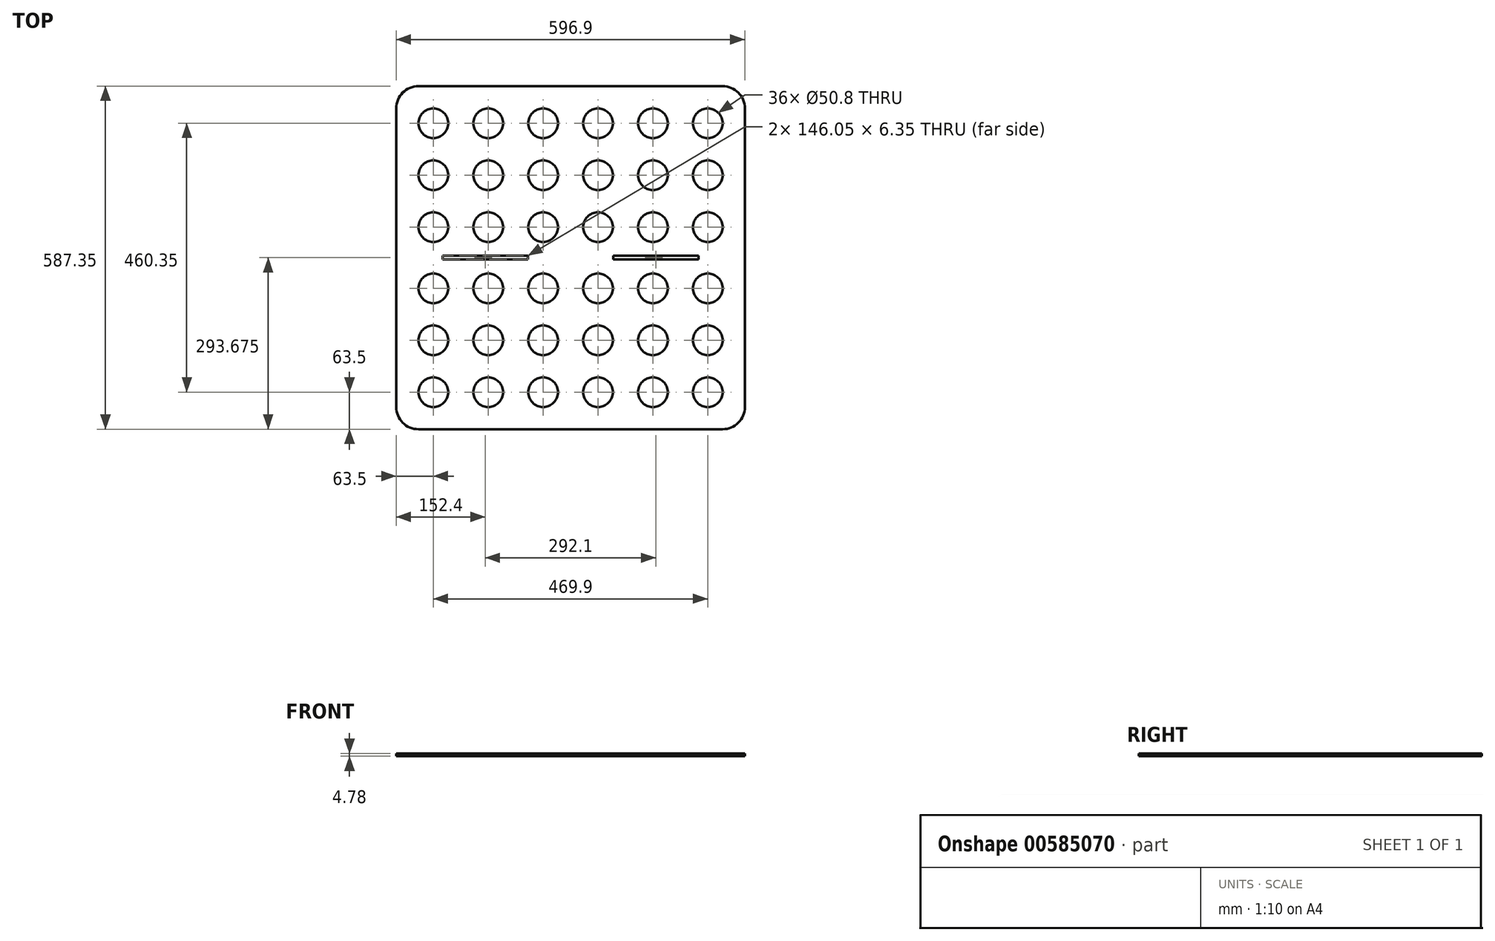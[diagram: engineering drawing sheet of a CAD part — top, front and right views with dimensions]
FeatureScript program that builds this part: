
annotation { "Feature Type Name" : "Feature", "Feature Type Description" : "" }
export const myFeature = defineFeature(function(context is Context, id is Id, definition is map)
    precondition{}
    {
        {
            var Q0;
            Q0=qCreatedBy(makeId("Top.planeOp"),FACE);
            var sketch = newSketch(context, id + "F0", { "sketchPlane" : qUnion([Q0])});
            skCircle(sketch, "E0", {"center": v(533.4, 346.05) * mm, "radius": 25.4 * mm});
            skLineSegment(sketch, "E1.bottom", {"start": v(0, 0) * mm, "end": v(596.9, 0) * mm});
            skLineSegment(sketch, "E1.top", {"start": v(0, 587.35) * mm, "end": v(596.9, 587.35) * mm});
            skLineSegment(sketch, "E1.left", {"start": v(0, 0) * mm, "end": v(0, 587.35) * mm});
            skLineSegment(sketch, "E1.right", {"start": v(596.9, 0) * mm, "end": v(596.9, 587.35) * mm});
            skLineSegment(sketch, "E2", {"start": v(298.45, 587.35) * mm, "end": v(298.45, 0) * mm, "construction": true});
            skCircle(sketch, "E3.1.0.1", {"center": v(439.42, 346.05) * mm, "radius": 25.4 * mm});
            skCircle(sketch, "E3.2.0.1", {"center": v(345.44, 346.05) * mm, "radius": 25.4 * mm});
            skCircle(sketch, "E3.3.0.1", {"center": v(251.46, 346.05) * mm, "radius": 25.4 * mm});
            skCircle(sketch, "E3.4.0.1", {"center": v(157.48, 346.05) * mm, "radius": 25.4 * mm});
            skCircle(sketch, "E3.5.0.1", {"center": v(63.5, 346.05) * mm, "radius": 25.4 * mm});
            skLineSegment(sketch, "E3.direction1", {"start": v(0, 0) * mm, "end": v(-88.9, 0) * mm, "construction": true});
            skLineSegment(sketch, "E4", {"start": v(0, 293.67) * mm, "end": v(596.9, 293.67) * mm, "construction": true});
            skCircle(sketch, "E5.0.1.0", {"center": v(157.48, 434.95) * mm, "radius": 25.4 * mm});
            skCircle(sketch, "E5.0.1.1", {"center": v(439.42, 434.95) * mm, "radius": 25.4 * mm});
            skCircle(sketch, "E5.0.1.2", {"center": v(251.46, 434.95) * mm, "radius": 25.4 * mm});
            skCircle(sketch, "E5.0.1.3", {"center": v(63.5, 434.95) * mm, "radius": 25.4 * mm});
            skCircle(sketch, "E5.0.1.4", {"center": v(533.4, 434.95) * mm, "radius": 25.4 * mm});
            skCircle(sketch, "E5.0.1.5", {"center": v(345.44, 434.95) * mm, "radius": 25.4 * mm});
            skCircle(sketch, "E5.0.2.0", {"center": v(157.48, 523.85) * mm, "radius": 25.4 * mm});
            skCircle(sketch, "E5.0.2.1", {"center": v(439.42, 523.85) * mm, "radius": 25.4 * mm});
            skCircle(sketch, "E5.0.2.2", {"center": v(251.46, 523.85) * mm, "radius": 25.4 * mm});
            skCircle(sketch, "E5.0.2.3", {"center": v(63.5, 523.85) * mm, "radius": 25.4 * mm});
            skCircle(sketch, "E5.0.2.4", {"center": v(533.4, 523.85) * mm, "radius": 25.4 * mm});
            skCircle(sketch, "E5.0.2.5", {"center": v(345.44, 523.85) * mm, "radius": 25.4 * mm});
            skLineSegment(sketch, "E5.direction1", {"start": v(63.5, 346.05) * mm, "end": v(88.9, 346.05) * mm, "construction": true});
            skLineSegment(sketch, "E5.direction2", {"start": v(63.5, 346.05) * mm, "end": v(63.5, 434.95) * mm, "construction": true});
            skCircle(sketch, "E6.0.1.0", {"center": v(439.42, 63.5) * mm, "radius": 25.4 * mm});
            skCircle(sketch, "E6.0.1.1", {"center": v(251.46, 241.3) * mm, "radius": 25.4 * mm});
            skLineSegment(sketch, "E6.0.1.2", {"start": v(63.5, 63.5) * mm, "end": v(63.5, 152.4) * mm, "construction": true});
            skCircle(sketch, "E6.0.1.3", {"center": v(345.44, 152.4) * mm, "radius": 25.4 * mm});
            skCircle(sketch, "E6.0.1.4", {"center": v(157.48, 241.3) * mm, "radius": 25.4 * mm});
            skCircle(sketch, "E6.0.1.5", {"center": v(251.46, 63.5) * mm, "radius": 25.4 * mm});
            skCircle(sketch, "E6.0.1.6", {"center": v(533.4, 63.5) * mm, "radius": 25.4 * mm});
            skCircle(sketch, "E6.0.1.7", {"center": v(439.42, 241.3) * mm, "radius": 25.4 * mm});
            skCircle(sketch, "E6.0.1.8", {"center": v(63.5, 241.3) * mm, "radius": 25.4 * mm});
            skCircle(sketch, "E6.0.1.9", {"center": v(345.44, 63.5) * mm, "radius": 25.4 * mm});
            skCircle(sketch, "E6.0.1.10", {"center": v(345.44, 241.3) * mm, "radius": 25.4 * mm});
            skCircle(sketch, "E6.0.1.11", {"center": v(439.42, 152.4) * mm, "radius": 25.4 * mm});
            skCircle(sketch, "E6.0.1.12", {"center": v(63.5, 152.4) * mm, "radius": 25.4 * mm});
            skCircle(sketch, "E6.0.1.13", {"center": v(157.48, 152.4) * mm, "radius": 25.4 * mm});
            skCircle(sketch, "E6.0.1.14", {"center": v(63.5, 63.5) * mm, "radius": 25.4 * mm});
            skCircle(sketch, "E6.0.1.15", {"center": v(533.4, 152.4) * mm, "radius": 25.4 * mm});
            skCircle(sketch, "E6.0.1.16", {"center": v(157.48, 63.5) * mm, "radius": 25.4 * mm});
            skCircle(sketch, "E6.0.1.17", {"center": v(251.46, 152.4) * mm, "radius": 25.4 * mm});
            skCircle(sketch, "E6.0.1.18", {"center": v(533.4, 241.3) * mm, "radius": 25.4 * mm});
            skLineSegment(sketch, "E6.0.1.19", {"start": v(63.5, 63.5) * mm, "end": v(88.9, 63.5) * mm, "construction": true});
            skLineSegment(sketch, "E6.0.1.20", {"start": v(63.5, 63.5) * mm, "end": v(88.9, 63.5) * mm, "construction": true});
            skLineSegment(sketch, "E6.direction2", {"start": v(63.5, 346.05) * mm, "end": v(63.5, 65.07) * mm, "construction": true});
            skSolve(sketch);
        }
        {
            var Q0;
            Q0 = qSketchRegion(id + "F0", true);
            extrude(context, id + "F1", {"entities" : qUnion([Q0]), "depth" : 4.78 * mm, "offsetDistance" : 25.4 * mm});
        }
        {
            var Q0;
            Q0=makeQuery(id+"F1.opExtrude","SWEPT_EDGE",EDGE,{"disambiguationData":[OSD([sQuery(id+"F0.wireOp",EDGE,"E1.bottom"),sQuery(id+"F0.wireOp",EDGE,"E1.left")])]});
            var Q1;
            Q1=makeQuery(id+"F1.opExtrude","SWEPT_EDGE",EDGE,{"disambiguationData":[OSD([sQuery(id+"F0.wireOp",EDGE,"E1.bottom"),sQuery(id+"F0.wireOp",EDGE,"E1.right")])]});
            var Q2;
            Q2=makeQuery(id+"F1.opExtrude","SWEPT_EDGE",EDGE,{"disambiguationData":[OSD([sQuery(id+"F0.wireOp",EDGE,"E1.top"),sQuery(id+"F0.wireOp",EDGE,"E1.right")])]});
            var Q3;
            Q3=makeQuery(id+"F1.opExtrude","SWEPT_EDGE",EDGE,{"disambiguationData":[OSD([sQuery(id+"F0.wireOp",EDGE,"E1.top"),sQuery(id+"F0.wireOp",EDGE,"E1.left")])]});
            fillet(context, id + "F2", {"entities" : qUnion([Q0, Q1, Q2, Q3]), "radius" : 38.1 * mm, "tangentPropagation" : true, "allowEdgeOverflow" : false});
        }
        {
            var Q0;
            Q0=makeQuery(id+"F1.opExtrude","CAP_FACE",FACE,{"disambiguationData":[OSD([sQuery(id+"F0.wireOp",EDGE,"E0"),sQuery(id+"F0.wireOp",EDGE,"E1.bottom"),sQuery(id+"F0.wireOp",EDGE,"E1.top"),sQuery(id+"F0.wireOp",EDGE,"E1.left"),sQuery(id+"F0.wireOp",EDGE,"E1.right"),sQuery(id+"F0.wireOp",EDGE,"E3.1.0.1"),sQuery(id+"F0.wireOp",EDGE,"E3.2.0.1"),sQuery(id+"F0.wireOp",EDGE,"E3.3.0.1"),sQuery(id+"F0.wireOp",EDGE,"E3.4.0.1"),sQuery(id+"F0.wireOp",EDGE,"E3.5.0.1"),sQuery(id+"F0.wireOp",EDGE,"E5.0.1.0"),sQuery(id+"F0.wireOp",EDGE,"E5.0.1.1"),sQuery(id+"F0.wireOp",EDGE,"E5.0.1.2"),sQuery(id+"F0.wireOp",EDGE,"E5.0.1.3"),sQuery(id+"F0.wireOp",EDGE,"E5.0.1.4"),sQuery(id+"F0.wireOp",EDGE,"E5.0.1.5"),sQuery(id+"F0.wireOp",EDGE,"E5.0.2.0"),sQuery(id+"F0.wireOp",EDGE,"E5.0.2.1"),sQuery(id+"F0.wireOp",EDGE,"E5.0.2.2"),sQuery(id+"F0.wireOp",EDGE,"E5.0.2.3"),sQuery(id+"F0.wireOp",EDGE,"E5.0.2.4"),sQuery(id+"F0.wireOp",EDGE,"E5.0.2.5"),sQuery(id+"F0.wireOp",EDGE,"4111b35f-3c82-41cd-824e-7dc98a569e06.0.1.0"),sQuery(id+"F0.wireOp",EDGE,"4111b35f-3c82-41cd-824e-7dc98a569e06.0.1.1"),sQuery(id+"F0.wireOp",EDGE,"4111b35f-3c82-41cd-824e-7dc98a569e06.0.1.3"),sQuery(id+"F0.wireOp",EDGE,"4111b35f-3c82-41cd-824e-7dc98a569e06.0.1.4"),sQuery(id+"F0.wireOp",EDGE,"4111b35f-3c82-41cd-824e-7dc98a569e06.0.1.5"),sQuery(id+"F0.wireOp",EDGE,"4111b35f-3c82-41cd-824e-7dc98a569e06.0.1.6"),sQuery(id+"F0.wireOp",EDGE,"4111b35f-3c82-41cd-824e-7dc98a569e06.0.1.7"),sQuery(id+"F0.wireOp",EDGE,"4111b35f-3c82-41cd-824e-7dc98a569e06.0.1.8"),sQuery(id+"F0.wireOp",EDGE,"4111b35f-3c82-41cd-824e-7dc98a569e06.0.1.9"),sQuery(id+"F0.wireOp",EDGE,"4111b35f-3c82-41cd-824e-7dc98a569e06.0.1.10"),sQuery(id+"F0.wireOp",EDGE,"4111b35f-3c82-41cd-824e-7dc98a569e06.0.1.11"),sQuery(id+"F0.wireOp",EDGE,"4111b35f-3c82-41cd-824e-7dc98a569e06.0.1.12"),sQuery(id+"F0.wireOp",EDGE,"4111b35f-3c82-41cd-824e-7dc98a569e06.0.1.13"),sQuery(id+"F0.wireOp",EDGE,"4111b35f-3c82-41cd-824e-7dc98a569e06.0.1.14"),sQuery(id+"F0.wireOp",EDGE,"4111b35f-3c82-41cd-824e-7dc98a569e06.0.1.15"),sQuery(id+"F0.wireOp",EDGE,"4111b35f-3c82-41cd-824e-7dc98a569e06.0.1.16"),sQuery(id+"F0.wireOp",EDGE,"4111b35f-3c82-41cd-824e-7dc98a569e06.0.1.17"),sQuery(id+"F0.wireOp",EDGE,"4111b35f-3c82-41cd-824e-7dc98a569e06.0.1.18")])],"isStart":false});
            var sketch = newSketch(context, id + "F3", { "sketchPlane" : qUnion([Q0])});
            skLineSegment(sketch, "E7", {"start": v(0, 293.67) * mm, "end": v(596.9, 293.67) * mm, "construction": true});
            skLineSegment(sketch, "E8", {"start": v(298.45, 587.35) * mm, "end": v(298.45, 293.67) * mm, "construction": true});
            skLineSegment(sketch, "E9.bottom", {"start": v(225.42, 296.85) * mm, "end": v(79.37, 296.85) * mm});
            skLineSegment(sketch, "E9.top", {"start": v(225.42, 290.5) * mm, "end": v(79.37, 290.5) * mm});
            skLineSegment(sketch, "E9.left", {"start": v(225.42, 296.85) * mm, "end": v(225.42, 290.5) * mm});
            skLineSegment(sketch, "E9.right", {"start": v(79.37, 296.85) * mm, "end": v(79.37, 290.5) * mm});
            skPoint(sketch, "E9.middle", {"position": v(152.4, 293.67) * mm});
            skLineSegment(sketch, "E10.1.0.0", {"start": v(517.52, 290.5) * mm, "end": v(371.47, 290.5) * mm});
            skLineSegment(sketch, "E10.1.0.1", {"start": v(517.52, 296.85) * mm, "end": v(371.47, 296.85) * mm});
            skPoint(sketch, "E10.1.0.2", {"position": v(439.17, 293.67) * mm});
            skLineSegment(sketch, "E10.1.0.3", {"start": v(517.52, 296.85) * mm, "end": v(517.52, 290.5) * mm});
            skLineSegment(sketch, "E10.1.0.4", {"start": v(371.47, 296.85) * mm, "end": v(371.47, 290.5) * mm});
            skSolve(sketch);
        }
        {
            var Q0;
            Q0 = qSketchRegion(id + "F3", true);
            extrude(context, id + "F4", {"entities" : qUnion([Q0]), "operationType" : NewBodyOperationType.REMOVE, "oppositeDirection" : true, "depth" : 25.4 * mm, "offsetDistance" : 25.4 * mm});
        }
    });
